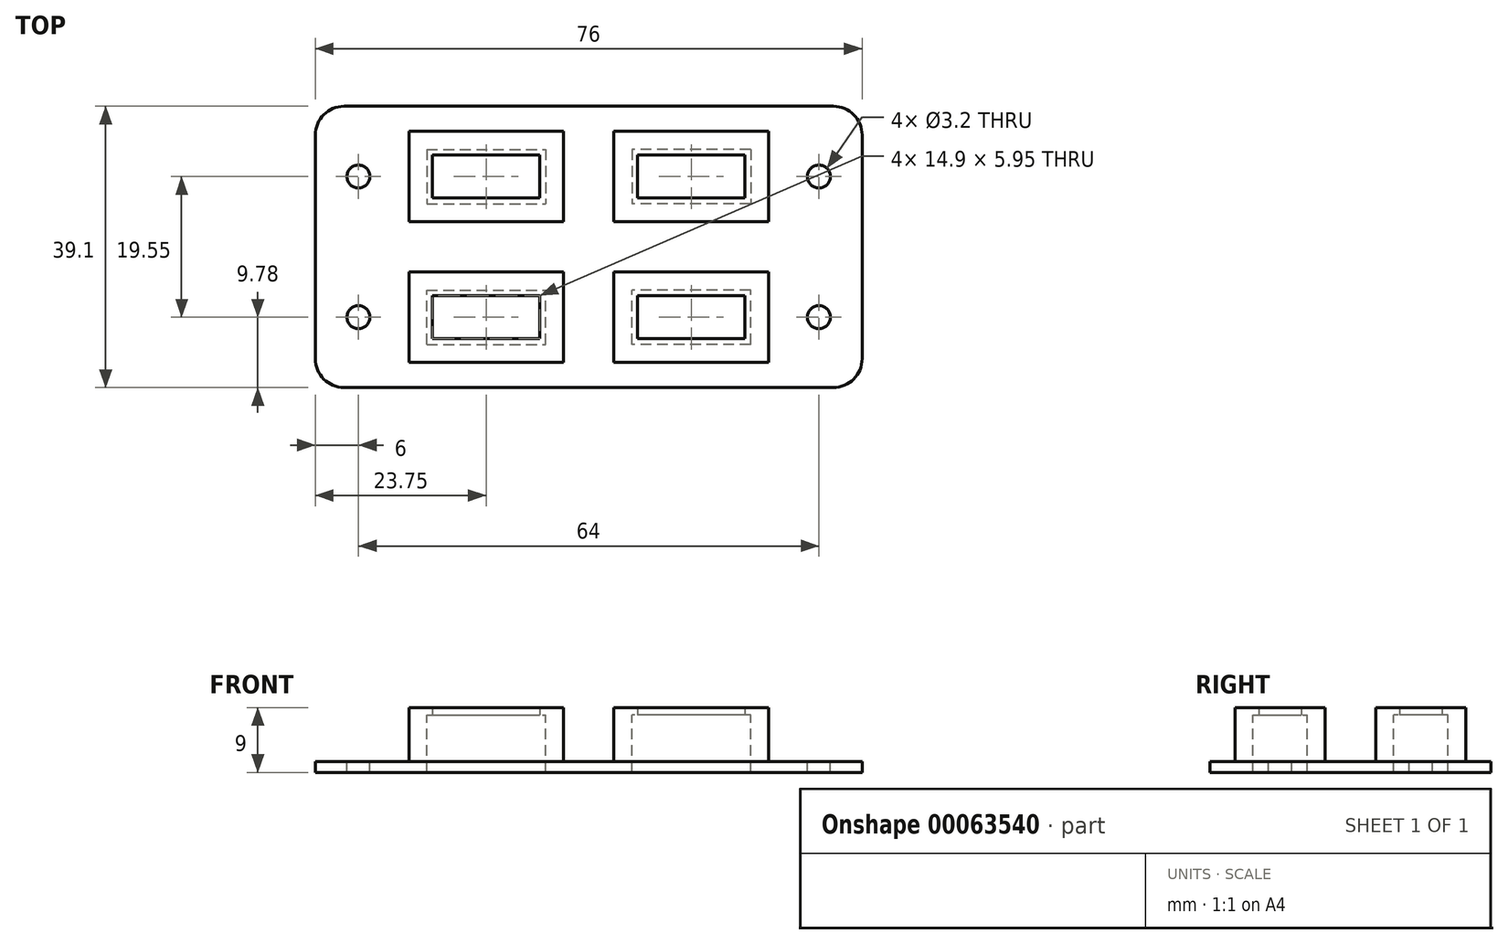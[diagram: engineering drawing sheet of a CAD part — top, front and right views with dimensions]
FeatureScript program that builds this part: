
annotation { "Feature Type Name" : "Feature", "Feature Type Description" : "" }
export const myFeature = defineFeature(function(context is Context, id is Id, definition is map)
    precondition{}
    {
        {
            var Q0;
            Q0=qCreatedBy(makeId("Top.planeOp"),FACE);
            var sketch = newSketch(context, id + "F0", { "sketchPlane" : qUnion([Q0])});
            skLineSegment(sketch, "E0.rect.bottom", {"start": v(8.25, -3.77) * mm, "end": v(-8.25, -3.78) * mm});
            skLineSegment(sketch, "E0.rect.top", {"start": v(8.25, 3.78) * mm, "end": v(-8.25, 3.77) * mm});
            skLineSegment(sketch, "E0.rect.left", {"start": v(8.25, -3.77) * mm, "end": v(8.25, 3.78) * mm});
            skLineSegment(sketch, "E0.rect.right", {"start": v(-8.25, -3.78) * mm, "end": v(-8.25, 3.78) * mm});
            skPoint(sketch, "E0.rect.middle", {"position": v(0, 0) * mm});
            skLineSegment(sketch, "E1.0", {"start": v(10.75, 6.28) * mm, "end": v(-10.75, 6.27) * mm});
            skLineSegment(sketch, "E1.1", {"start": v(10.75, -6.27) * mm, "end": v(10.75, 6.28) * mm});
            skLineSegment(sketch, "E1.2", {"start": v(10.75, -6.27) * mm, "end": v(-10.75, -6.28) * mm});
            skLineSegment(sketch, "E1.3", {"start": v(-10.75, -6.28) * mm, "end": v(-10.75, 6.27) * mm});
            skLineSegment(sketch, "E2", {"start": v(-14.25, 132.31) * mm, "end": v(-14.25, -85.37) * mm, "construction": true});
            skLineSegment(sketch, "E3.MirrorCS", {"start": v(-39.25, 6.28) * mm, "end": v(-17.75, 6.28) * mm});
            skLineSegment(sketch, "E4.MirrorCS", {"start": v(-36.75, 3.78) * mm, "end": v(-20.25, 3.78) * mm});
            skLineSegment(sketch, "E5.MirrorCS", {"start": v(-17.75, -6.28) * mm, "end": v(-17.75, 6.27) * mm});
            skLineSegment(sketch, "E6.MirrorCS", {"start": v(-20.25, -3.78) * mm, "end": v(-20.25, 3.78) * mm});
            skLineSegment(sketch, "E7.MirrorCS", {"start": v(-39.25, -6.28) * mm, "end": v(-17.75, -6.27) * mm});
            skLineSegment(sketch, "E8.MirrorCS", {"start": v(-36.75, -3.77) * mm, "end": v(-20.25, -3.77) * mm});
            skLineSegment(sketch, "E9.MirrorCS", {"start": v(-36.75, -3.77) * mm, "end": v(-36.75, 3.78) * mm});
            skLineSegment(sketch, "E10.MirrorCS", {"start": v(-39.25, -6.27) * mm, "end": v(-39.25, 6.28) * mm});
            skLineSegment(sketch, "E11", {"start": v(-14.25, 9.78) * mm, "end": v(17.75, 9.78) * mm, "construction": true});
            skLineSegment(sketch, "E12", {"start": v(17.75, 9.78) * mm, "end": v(17.75, -9.78) * mm, "construction": true});
            skLineSegment(sketch, "E13", {"start": v(17.75, -9.77) * mm, "end": v(-14.25, -9.78) * mm});
            skCircle(sketch, "E14", {"center": v(17.75, 0) * mm, "radius": 1.6 * mm});
            skLineSegment(sketch, "E15.MirrorCS", {"start": v(-14.25, 9.78) * mm, "end": v(-46.25, 9.78) * mm, "construction": true});
            skLineSegment(sketch, "E16.MirrorCS", {"start": v(-46.25, -9.78) * mm, "end": v(-14.25, -9.77) * mm});
            skCircle(sketch, "E17.MirrorC", {"center": v(-46.25, 0) * mm, "radius": 1.6 * mm});
            skLineSegment(sketch, "E18.MirrorCS", {"start": v(-39.25, 25.83) * mm, "end": v(-17.75, 25.83) * mm});
            skLineSegment(sketch, "E19.MirrorCS", {"start": v(-36.75, 23.33) * mm, "end": v(-20.25, 23.33) * mm});
            skLineSegment(sketch, "E20.MirrorCS", {"start": v(-36.75, 23.33) * mm, "end": v(-36.75, 15.78) * mm});
            skLineSegment(sketch, "E21.MirrorCS", {"start": v(8.25, 23.33) * mm, "end": v(-8.25, 23.33) * mm});
            skLineSegment(sketch, "E22.MirrorCS", {"start": v(8.25, 15.78) * mm, "end": v(-8.25, 15.78) * mm});
            skLineSegment(sketch, "E23.MirrorCS", {"start": v(-8.25, 23.33) * mm, "end": v(-8.25, 15.78) * mm});
            skPoint(sketch, "E24.MirrorP", {"position": v(0, 19.55) * mm});
            skLineSegment(sketch, "E25.MirrorCS", {"start": v(10.75, 25.83) * mm, "end": v(-10.75, 25.83) * mm});
            skLineSegment(sketch, "E26.MirrorCS", {"start": v(-36.75, 15.78) * mm, "end": v(-20.25, 15.78) * mm});
            skLineSegment(sketch, "E27.MirrorCS", {"start": v(10.75, 13.28) * mm, "end": v(-10.75, 13.28) * mm});
            skLineSegment(sketch, "E28.MirrorCS", {"start": v(10.75, 25.83) * mm, "end": v(10.75, 13.28) * mm});
            skLineSegment(sketch, "E29.MirrorCS", {"start": v(-39.25, 13.28) * mm, "end": v(-17.75, 13.28) * mm});
            skLineSegment(sketch, "E30.MirrorCS", {"start": v(-10.75, 25.83) * mm, "end": v(-10.75, 13.28) * mm});
            skLineSegment(sketch, "E31.MirrorCS", {"start": v(-20.25, 23.33) * mm, "end": v(-20.25, 15.78) * mm});
            skLineSegment(sketch, "E32.MirrorCS", {"start": v(-39.25, 25.83) * mm, "end": v(-39.25, 13.28) * mm});
            skLineSegment(sketch, "E33.MirrorCS", {"start": v(-17.75, 25.83) * mm, "end": v(-17.75, 13.28) * mm});
            skLineSegment(sketch, "E34.MirrorCS", {"start": v(8.25, 23.33) * mm, "end": v(8.25, 15.78) * mm});
            skCircle(sketch, "E35.MirrorC", {"center": v(-46.25, 19.55) * mm, "radius": 1.6 * mm});
            skCircle(sketch, "E36.MirrorC", {"center": v(17.75, 19.55) * mm, "radius": 1.6 * mm});
            skLineSegment(sketch, "E37.MirrorCS", {"start": v(-46.25, 29.33) * mm, "end": v(-14.25, 29.33) * mm});
            skLineSegment(sketch, "E38.MirrorCS", {"start": v(17.75, 29.33) * mm, "end": v(-14.25, 29.33) * mm});
            skLineSegment(sketch, "E39", {"start": v(-52.25, 25.32) * mm, "end": v(-52.25, -5.77) * mm});
            skLineSegment(sketch, "E40", {"start": v(-48.25, -9.77) * mm, "end": v(-46.25, -9.77) * mm});
            skLineSegment(sketch, "E41", {"start": v(-48.25, 29.33) * mm, "end": v(-46.25, 29.33) * mm});
            skLineSegment(sketch, "E42.MirrorCS", {"start": v(19.75, 29.33) * mm, "end": v(17.75, 29.33) * mm});
            skLineSegment(sketch, "E43.MirrorCS", {"start": v(23.75, 25.33) * mm, "end": v(23.75, -5.78) * mm});
            skLineSegment(sketch, "E44.MirrorCS", {"start": v(19.75, -9.78) * mm, "end": v(17.75, -9.78) * mm});
            skPoint(sketch, "E45.visualSharp", {"position": v(-52.25, 29.33) * mm});
            skArc(sketch, "E45.filletArc", {"start": v(-48.25, 29.32) * mm, "mid": v(-51.08, 28.15) * mm, "end": v(-52.25, 25.32) * mm});
            skPoint(sketch, "E46.visualSharp", {"position": v(-52.25, -9.78) * mm});
            skArc(sketch, "E46.filletArc", {"start": v(-52.25, -5.77) * mm, "mid": v(-51.08, -8.6) * mm, "end": v(-48.25, -9.77) * mm});
            skPoint(sketch, "E47.visualSharp", {"position": v(23.75, 29.33) * mm});
            skArc(sketch, "E47.filletArc", {"start": v(23.75, 25.33) * mm, "mid": v(22.58, 28.15) * mm, "end": v(19.75, 29.33) * mm});
            skPoint(sketch, "E48.visualSharp", {"position": v(23.75, -9.78) * mm});
            skArc(sketch, "E48.filletArc", {"start": v(19.75, -9.78) * mm, "mid": v(22.58, -8.6) * mm, "end": v(23.75, -5.78) * mm});
            skSolve(sketch);
        }
        {
            var Q0;
            Q0=makeQuery(id+"F0.imprint","IMPRINT",FACE,{"disambiguationData":[TD([[makeQuery(id+"F0.imprint","IMPRINT",EDGE,{"derivedFrom":sQuery(id+"F0.wireOp",EDGE,"E1.0")}),-1.0]])]});
            var Q1;
            Q1=makeQuery(id+"F0.imprint","IMPRINT",FACE,{"disambiguationData":[TD([[makeQuery(id+"F0.imprint","IMPRINT",EDGE,{"derivedFrom":sQuery(id+"F0.wireOp",EDGE,"E3.MirrorCS")}),-1.0]])]});
            var Q2;
            Q2=makeQuery(id+"F0.imprint","IMPRINT",FACE,{"disambiguationData":[TD([[makeQuery(id+"F0.imprint","IMPRINT",EDGE,{"derivedFrom":sQuery(id+"F0.wireOp",EDGE,"E0.rect.bottom")}),1.0]])]});
            var Q3;
            Q3=makeQuery(id+"F0.imprint","IMPRINT",FACE,{"disambiguationData":[TD([[makeQuery(id+"F0.imprint","IMPRINT",EDGE,{"derivedFrom":sQuery(id+"F0.wireOp",EDGE,"E18.MirrorCS")}),-1.0]])]});
            var Q4;
            Q4=makeQuery(id+"F0.imprint","IMPRINT",FACE,{"disambiguationData":[TD([[makeQuery(id+"F0.imprint","IMPRINT",EDGE,{"derivedFrom":sQuery(id+"F0.wireOp",EDGE,"E21.MirrorCS")}),-1.0]])]});
            extrude(context, id + "F1", {"entities" : qUnion([Q0, Q1, Q2, Q3, Q4]), "oppositeDirection" : true, "depth" : 1.5 * mm});
        }
        {
            var Q0;
            Q0=makeQuery(id+"F0.imprint","IMPRINT",FACE,{"disambiguationData":[TD([[makeQuery(id+"F0.imprint","IMPRINT",EDGE,{"derivedFrom":sQuery(id+"F0.wireOp",EDGE,"E0.rect.bottom")}),1.0]])]});
            var Q1;
            Q1=makeQuery(id+"F0.imprint","IMPRINT",FACE,{"disambiguationData":[TD([[makeQuery(id+"F0.imprint","IMPRINT",EDGE,{"derivedFrom":sQuery(id+"F0.wireOp",EDGE,"E3.MirrorCS")}),-1.0]])]});
            var Q2;
            Q2=makeQuery(id+"F0.imprint","IMPRINT",FACE,{"disambiguationData":[TD([[makeQuery(id+"F0.imprint","IMPRINT",EDGE,{"derivedFrom":sQuery(id+"F0.wireOp",EDGE,"E18.MirrorCS")}),-1.0]])]});
            var Q3;
            Q3=makeQuery(id+"F0.imprint","IMPRINT",FACE,{"disambiguationData":[TD([[makeQuery(id+"F0.imprint","IMPRINT",EDGE,{"derivedFrom":sQuery(id+"F0.wireOp",EDGE,"E21.MirrorCS")}),-1.0]])]});
            extrude(context, id + "F2", {"entities" : qUnion([Q0, Q1, Q2, Q3]), "operationType" : NewBodyOperationType.ADD, "depth" : 6.5 * mm});
        }
        {
            var Q0;
            Q0=makeQuery(id+"F2.opExtrude","CAP_FACE",FACE,{"disambiguationData":[OSD([sQuery(id+"F0.wireOp",EDGE,"E0.rect.bottom"),sQuery(id+"F0.wireOp",EDGE,"E0.rect.top"),sQuery(id+"F0.wireOp",EDGE,"E0.rect.left"),sQuery(id+"F0.wireOp",EDGE,"E0.rect.right"),sQuery(id+"F0.wireOp",EDGE,"E1.0"),sQuery(id+"F0.wireOp",EDGE,"E1.1"),sQuery(id+"F0.wireOp",EDGE,"E1.2"),sQuery(id+"F0.wireOp",EDGE,"E1.3")])],"isStart":false});
            var sketch = newSketch(context, id + "F3", { "sketchPlane" : qUnion([Q0])});
            skLineSegment(sketch, "E49.0", {"start": v(10.75, 6.28) * mm, "end": v(-10.75, 6.27) * mm});
            skLineSegment(sketch, "E50.0", {"start": v(-10.75, -6.28) * mm, "end": v(-10.75, 6.27) * mm});
            skLineSegment(sketch, "E51.0", {"start": v(10.75, -6.27) * mm, "end": v(-10.75, -6.28) * mm});
            skLineSegment(sketch, "E52.0", {"start": v(10.75, -6.27) * mm, "end": v(10.75, 6.28) * mm});
            skLineSegment(sketch, "E53.0", {"start": v(8.25, 3.78) * mm, "end": v(-8.25, 3.77) * mm});
            skLineSegment(sketch, "E54.0", {"start": v(-8.25, -3.78) * mm, "end": v(-8.25, 3.77) * mm});
            skLineSegment(sketch, "E55.0", {"start": v(8.25, -3.77) * mm, "end": v(-8.25, -3.78) * mm});
            skLineSegment(sketch, "E56.0", {"start": v(8.25, -3.77) * mm, "end": v(8.25, 3.78) * mm});
            skLineSegment(sketch, "E57.0", {"start": v(7.45, 2.98) * mm, "end": v(-7.45, 2.97) * mm});
            skLineSegment(sketch, "E57.1", {"start": v(7.45, -2.97) * mm, "end": v(7.45, 2.98) * mm});
            skLineSegment(sketch, "E57.2", {"start": v(7.45, -2.97) * mm, "end": v(-7.45, -2.98) * mm});
            skLineSegment(sketch, "E57.3", {"start": v(-7.45, -2.97) * mm, "end": v(-7.45, 2.98) * mm});
            skLineSegment(sketch, "E58.0", {"start": v(-14.25, 132.31) * mm, "end": v(-14.25, -85.37) * mm, "construction": true});
            skLineSegment(sketch, "E59.MirrorCS", {"start": v(-39.25, 6.28) * mm, "end": v(-17.75, 6.28) * mm});
            skLineSegment(sketch, "E60.MirrorCS", {"start": v(-36.75, 3.78) * mm, "end": v(-20.25, 3.78) * mm});
            skLineSegment(sketch, "E61.MirrorCS", {"start": v(-35.95, 2.98) * mm, "end": v(-21.05, 2.98) * mm});
            skLineSegment(sketch, "E62.MirrorCS", {"start": v(-17.75, -6.28) * mm, "end": v(-17.75, 6.27) * mm});
            skLineSegment(sketch, "E63.MirrorCS", {"start": v(-20.25, -3.77) * mm, "end": v(-20.25, 3.77) * mm});
            skLineSegment(sketch, "E64.MirrorCS", {"start": v(-21.05, -2.97) * mm, "end": v(-21.05, 2.98) * mm});
            skLineSegment(sketch, "E65.MirrorCS", {"start": v(-39.25, -6.27) * mm, "end": v(-17.75, -6.27) * mm});
            skLineSegment(sketch, "E66.MirrorCS", {"start": v(-36.75, -3.77) * mm, "end": v(-20.25, -3.77) * mm});
            skLineSegment(sketch, "E67.MirrorCS", {"start": v(-35.95, -2.97) * mm, "end": v(-21.05, -2.97) * mm});
            skLineSegment(sketch, "E68.MirrorCS", {"start": v(-35.95, -2.97) * mm, "end": v(-35.95, 2.98) * mm});
            skLineSegment(sketch, "E69.MirrorCS", {"start": v(-36.75, -3.77) * mm, "end": v(-36.75, 3.78) * mm});
            skLineSegment(sketch, "E70.MirrorCS", {"start": v(-39.25, -6.27) * mm, "end": v(-39.25, 6.28) * mm});
            skLineSegment(sketch, "E71.0", {"start": v(-52.25, 25.32) * mm, "end": v(-52.25, -5.77) * mm});
            skLineSegment(sketch, "E72.0", {"start": v(23.75, 25.33) * mm, "end": v(23.75, -5.78) * mm});
            skLineSegment(sketch, "E73", {"start": v(-52.25, 9.77) * mm, "end": v(23.75, 9.78) * mm, "construction": true});
            skLineSegment(sketch, "E74.MirrorCS", {"start": v(-36.75, 23.32) * mm, "end": v(-36.75, 15.77) * mm});
            skLineSegment(sketch, "E75.MirrorCS", {"start": v(-36.75, 15.77) * mm, "end": v(-20.25, 15.77) * mm});
            skLineSegment(sketch, "E76.MirrorCS", {"start": v(-10.75, 25.82) * mm, "end": v(-10.75, 13.28) * mm});
            skLineSegment(sketch, "E77.MirrorCS", {"start": v(10.75, 25.82) * mm, "end": v(10.75, 13.27) * mm});
            skLineSegment(sketch, "E78.MirrorCS", {"start": v(-36.75, 23.32) * mm, "end": v(-20.25, 23.32) * mm});
            skLineSegment(sketch, "E79.MirrorCS", {"start": v(-21.05, 22.52) * mm, "end": v(-21.05, 16.57) * mm});
            skLineSegment(sketch, "E80.MirrorCS", {"start": v(8.25, 23.32) * mm, "end": v(-8.25, 23.33) * mm});
            skLineSegment(sketch, "E81.MirrorCS", {"start": v(-35.95, 22.52) * mm, "end": v(-21.05, 22.52) * mm});
            skLineSegment(sketch, "E82.MirrorCS", {"start": v(-20.25, 23.32) * mm, "end": v(-20.25, 15.77) * mm});
            skLineSegment(sketch, "E83.MirrorCS", {"start": v(10.75, 25.82) * mm, "end": v(-10.75, 25.82) * mm});
            skLineSegment(sketch, "E84.MirrorCS", {"start": v(8.25, 23.32) * mm, "end": v(8.25, 15.77) * mm});
            skLineSegment(sketch, "E85.MirrorCS", {"start": v(7.45, 16.57) * mm, "end": v(-7.45, 16.57) * mm});
            skLineSegment(sketch, "E86.MirrorCS", {"start": v(7.45, 22.52) * mm, "end": v(7.45, 16.57) * mm});
            skLineSegment(sketch, "E87.MirrorCS", {"start": v(7.45, 22.52) * mm, "end": v(-7.45, 22.52) * mm});
            skLineSegment(sketch, "E88.MirrorCS", {"start": v(-7.45, 22.52) * mm, "end": v(-7.45, 16.57) * mm});
            skLineSegment(sketch, "E89.MirrorCS", {"start": v(8.25, 15.77) * mm, "end": v(-8.25, 15.77) * mm});
            skLineSegment(sketch, "E90.MirrorCS", {"start": v(-39.25, 25.82) * mm, "end": v(-17.75, 25.82) * mm});
            skLineSegment(sketch, "E91.MirrorCS", {"start": v(-8.25, 23.32) * mm, "end": v(-8.25, 15.78) * mm});
            skLineSegment(sketch, "E92.MirrorCS", {"start": v(-17.75, 25.82) * mm, "end": v(-17.75, 13.27) * mm});
            skLineSegment(sketch, "E93.MirrorCS", {"start": v(-35.95, 22.52) * mm, "end": v(-35.95, 16.57) * mm});
            skLineSegment(sketch, "E94.MirrorCS", {"start": v(10.75, 13.27) * mm, "end": v(-10.75, 13.27) * mm});
            skLineSegment(sketch, "E95.MirrorCS", {"start": v(-39.25, 25.82) * mm, "end": v(-39.25, 13.27) * mm});
            skLineSegment(sketch, "E96.MirrorCS", {"start": v(-35.95, 16.57) * mm, "end": v(-21.05, 16.57) * mm});
            skLineSegment(sketch, "E97.MirrorCS", {"start": v(-39.25, 13.27) * mm, "end": v(-17.75, 13.27) * mm});
            skSolve(sketch);
        }
        {
            var Q0;
            Q0=makeQuery(id+"F3.imprint","IMPRINT",FACE,{"disambiguationData":[TD([[makeQuery(id+"F3.imprint","IMPRINT",EDGE,{"derivedFrom":sQuery(id+"F3.wireOp",EDGE,"E59.MirrorCS")}),-1.0]])]});
            var Q1;
            Q1=makeQuery(id+"F3.imprint","IMPRINT",FACE,{"disambiguationData":[TD([[makeQuery(id+"F3.imprint","IMPRINT",EDGE,{"derivedFrom":sQuery(id+"F3.wireOp",EDGE,"E60.MirrorCS")}),-1.0]])]});
            var Q2;
            Q2=makeQuery(id+"F3.imprint","IMPRINT",FACE,{"disambiguationData":[TD([[makeQuery(id+"F3.imprint","IMPRINT",EDGE,{"derivedFrom":sQuery(id+"F3.wireOp",EDGE,"E49.0")}),1.0]])]});
            var Q3;
            Q3=makeQuery(id+"F3.imprint","IMPRINT",FACE,{"disambiguationData":[TD([[makeQuery(id+"F3.imprint","IMPRINT",EDGE,{"derivedFrom":sQuery(id+"F3.wireOp",EDGE,"E53.0")}),1.0]])]});
            var Q4;
            Q4=makeQuery(id+"F3.imprint","IMPRINT",FACE,{"disambiguationData":[TD([[makeQuery(id+"F3.imprint","IMPRINT",EDGE,{"derivedFrom":sQuery(id+"F3.wireOp",EDGE,"E74.MirrorCS")}),1.0]])]});
            var Q5;
            Q5=makeQuery(id+"F3.imprint","IMPRINT",FACE,{"disambiguationData":[TD([[makeQuery(id+"F3.imprint","IMPRINT",EDGE,{"derivedFrom":sQuery(id+"F3.wireOp",EDGE,"E74.MirrorCS")}),-1.0]])]});
            var Q6;
            Q6=makeQuery(id+"F3.imprint","IMPRINT",FACE,{"disambiguationData":[TD([[makeQuery(id+"F3.imprint","IMPRINT",EDGE,{"derivedFrom":sQuery(id+"F3.wireOp",EDGE,"E80.MirrorCS")}),1.0]])]});
            var Q7;
            Q7=makeQuery(id+"F3.imprint","IMPRINT",FACE,{"disambiguationData":[TD([[makeQuery(id+"F3.imprint","IMPRINT",EDGE,{"derivedFrom":sQuery(id+"F3.wireOp",EDGE,"E76.MirrorCS")}),1.0]])]});
            extrude(context, id + "F4", {"entities" : qUnion([Q0, Q1, Q2, Q3, Q4, Q5, Q6, Q7]), "operationType" : NewBodyOperationType.ADD, "depth" : 1 * mm});
        }
    });
